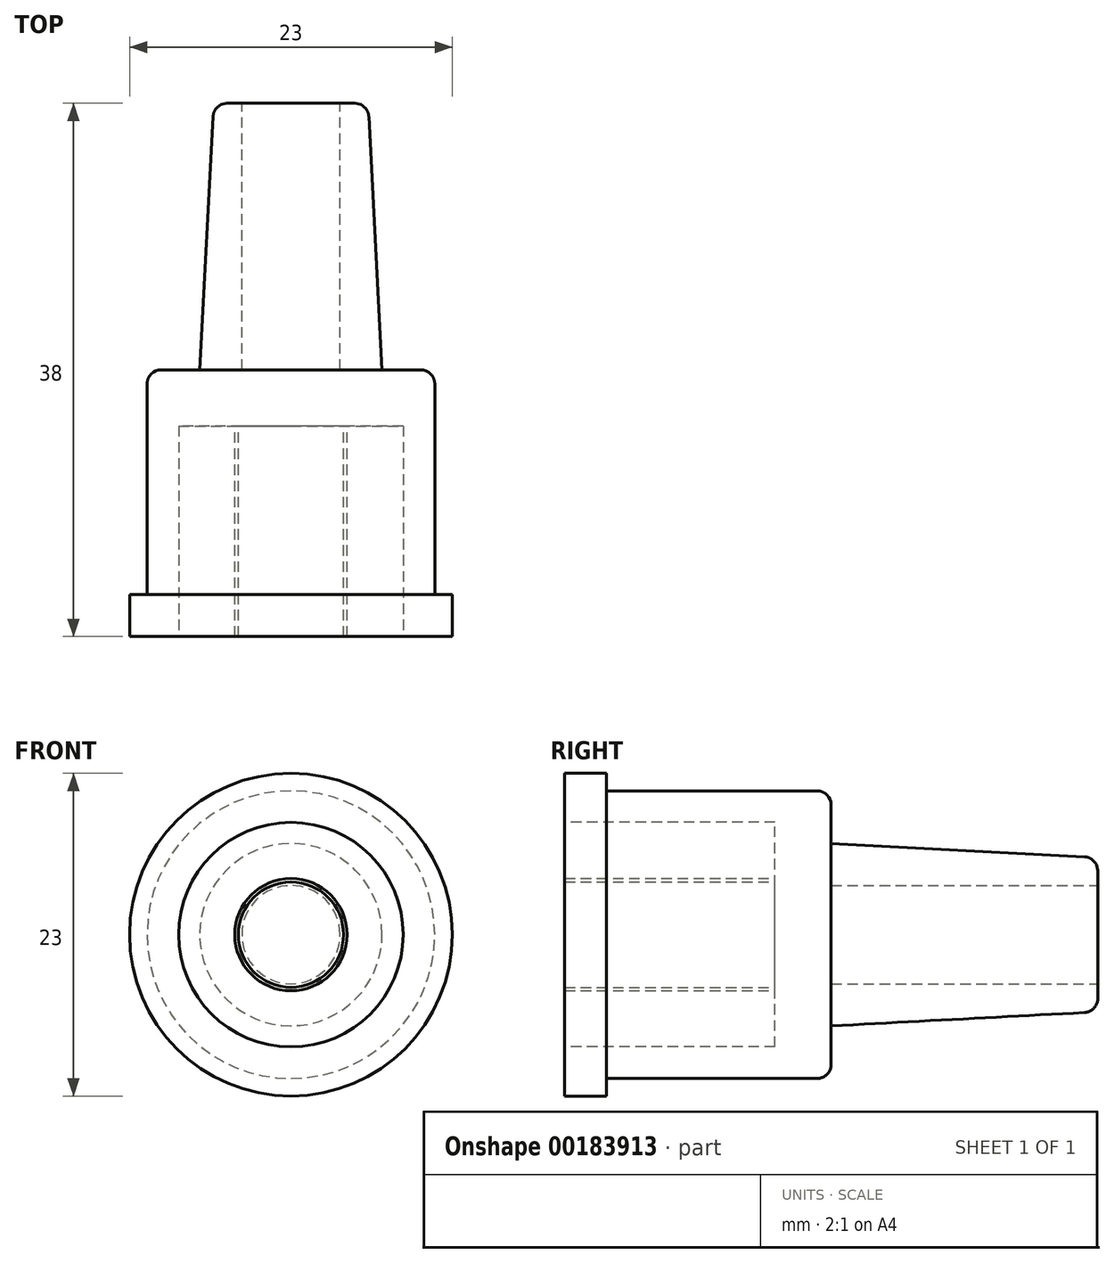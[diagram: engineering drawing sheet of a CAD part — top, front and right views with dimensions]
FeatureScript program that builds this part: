
annotation { "Feature Type Name" : "Feature", "Feature Type Description" : "" }
export const myFeature = defineFeature(function(context is Context, id is Id, definition is map)
    precondition{}
    {
        {
            var Q0;
            Q0=qCreatedBy(makeId("Front.planeOp"),FACE);
            var sketch = newSketch(context, id + "F0", { "sketchPlane" : qUnion([Q0])});
            skCircle(sketch, "E0", {"center": v(0, 0) * mm, "radius": 5.5 * mm});
            skSolve(sketch);
        }
        {
            var Q0;
            Q0=qCreatedBy(makeId("Front.planeOp"),FACE);
            cPlane(context, id + "F1", {"entities" : qUnion([Q0]), "cplaneType" : CPlaneType.OFFSET, "offset" : 19 * mm, "width" : 150 * mm, "height" : 150 * mm});
        }
        {
            var Q0;
            Q0=qCreatedBy(id+"F1.planeOp",FACE);
            var sketch = newSketch(context, id + "F2", { "sketchPlane" : qUnion([Q0])});
            skCircle(sketch, "E1", {"center": v(0, 0) * mm, "radius": 6.5 * mm});
            skSolve(sketch);
        }
        {
            var Q0;
            Q0=makeQuery(id+"F2.imprint","IMPRINT",FACE,{"disambiguationData":[TD([[makeQuery(id+"F2.imprint","IMPRINT",EDGE,{"derivedFrom":sQuery(id+"F2.wireOp",EDGE,"E1")}),1.0]])]});
            var Q1;
            Q1=makeQuery(id+"F0.imprint","IMPRINT",FACE,{"disambiguationData":[TD([[makeQuery(id+"F0.imprint","IMPRINT",EDGE,{"derivedFrom":sQuery(id+"F0.wireOp",EDGE,"E0")}),1.0]])]});
            loft(context, id + "F3", {"sheetProfilesArray" : [{ "sheetProfileEntities" : qUnion([Q0]) }, { "sheetProfileEntities" : qUnion([Q1]) }]});
        }
        {
            var Q0;
            Q0=makeQuery(id+"F3.opLoft","CAP_FACE",FACE,{"disambiguationData":[OSD([makeQuery(id+"F2.imprint","IMPRINT",FACE,{"disambiguationData":[TD([[makeQuery(id+"F2.imprint","IMPRINT",EDGE,{"derivedFrom":sQuery(id+"F2.wireOp",EDGE,"E1")}),1.0]])]})])],"isStart":true});
            var sketch = newSketch(context, id + "F4", { "sketchPlane" : qUnion([Q0])});
            skCircle(sketch, "E2", {"center": v(0, 0) * mm, "radius": 10.25 * mm});
            skSolve(sketch);
        }
        {
            var Q0;
            Q0 = qSketchRegion(id + "F4", true);
            extrude(context, id + "F5", {"entities" : qUnion([Q0]), "operationType" : NewBodyOperationType.ADD, "depth" : 19 * mm});
        }
        {
            var Q0;
            Q0=makeQuery(id+"F5.opExtrude","CAP_FACE",FACE,{"disambiguationData":[OSD([sQuery(id+"F4.wireOp",EDGE,"E2")])],"isStart":false});
            var sketch = newSketch(context, id + "F6", { "sketchPlane" : qUnion([Q0])});
            skCircle(sketch, "E3", {"center": v(0, 0) * mm, "radius": 11.5 * mm});
            skSolve(sketch);
        }
        {
            var Q0;
            Q0 = qSketchRegion(id + "F6", true);
            extrude(context, id + "F7", {"entities" : qUnion([Q0]), "operationType" : NewBodyOperationType.ADD, "oppositeDirection" : true, "depth" : 3 * mm});
        }
        {
            var Q0;
            Q0=makeQuery(id+"F3.opLoft","CAP_FACE",FACE,{"disambiguationData":[OSD([makeQuery(id+"F0.imprint","IMPRINT",FACE,{"disambiguationData":[TD([[makeQuery(id+"F0.imprint","IMPRINT",EDGE,{"derivedFrom":sQuery(id+"F0.wireOp",EDGE,"E0")}),1.0]])]})])],"isStart":true});
            var sketch = newSketch(context, id + "F8", { "sketchPlane" : qUnion([Q0])});
            skCircle(sketch, "E4", {"center": v(0, 0) * mm, "radius": 3.5 * mm});
            skSolve(sketch);
        }
        {
            var Q0;
            Q0 = qSketchRegion(id + "F8", true);
            extrude(context, id + "F9", {"entities" : qUnion([Q0]), "operationType" : NewBodyOperationType.REMOVE, "oppositeDirection" : true, "depth" : 19 * mm});
        }
        {
            var Q0;
            Q0=makeQuery(id+"F7.boolean.opBoolean","MERGE",FACE,{"derivedFrom":[makeQuery(id+"F5.opExtrude","CAP_FACE",FACE,{"disambiguationData":[OSD([sQuery(id+"F4.wireOp",EDGE,"E2")])],"isStart":false}),makeQuery(id+"F7.opExtrude","CAP_FACE",FACE,{"disambiguationData":[OSD([sQuery(id+"F6.wireOp",EDGE,"E3")])],"isStart":true})]});
            var sketch = newSketch(context, id + "F10", { "sketchPlane" : qUnion([Q0])});
            skCircle(sketch, "E5", {"center": v(0, 0) * mm, "radius": 8 * mm});
            skSolve(sketch);
        }
        {
            var Q0;
            Q0=makeQuery(id+"F10.imprint","IMPRINT",FACE,{"disambiguationData":[TD([[makeQuery(id+"F10.imprint","IMPRINT",EDGE,{"derivedFrom":sQuery(id+"F10.wireOp",EDGE,"E5")}),1.0]])]});
            extrude(context, id + "F11", {"entities" : qUnion([Q0]), "operationType" : NewBodyOperationType.REMOVE, "oppositeDirection" : true, "depth" : 15 * mm});
        }
        {
            var Q0;
            Q0=makeQuery(id+"F11.boolean.opBoolean","COPY",FACE,{"derivedFrom":makeQuery(id+"F11.opExtrude","CAP_FACE",FACE,{"disambiguationData":[OSD([sQuery(id+"F10.wireOp",EDGE,"E5")])],"isStart":false})});
            var sketch = newSketch(context, id + "F12", { "sketchPlane" : qUnion([Q0])});
            skCircle(sketch, "E6", {"center": v(0, 0) * mm, "radius": 4 * mm});
            skCircle(sketch, "E7", {"center": v(0, 0) * mm, "radius": 3.75 * mm});
            skSolve(sketch);
        }
        {
            var Q0;
            Q0=makeQuery(id+"F12.imprint","IMPRINT",FACE,{"disambiguationData":[TD([[makeQuery(id+"F12.imprint","IMPRINT",EDGE,{"derivedFrom":sQuery(id+"F12.wireOp",EDGE,"E6")}),1.0]])]});
            extrude(context, id + "F13", {"entities" : qUnion([Q0]), "depth" : 15 * mm});
        }
        {
            var Q0;
            Q0=makeQuery(id+"F3.opLoft","MID_CAP_EDGE",EDGE,{"disambiguationData":[OSD([sQuery(id+"F0.wireOp",EDGE,"E0"),sQuery(id+"F2.wireOp",EDGE,"E1")])],"capPos":1.0});
            var Q1;
            Q1=makeQuery(id+"F5.opExtrude","CAP_EDGE",EDGE,{"disambiguationData":[OSD([sQuery(id+"F4.wireOp",EDGE,"E2")])],"isStart":true});
            var Q2;
            Q2=makeQuery(id+"F3.opLoft","MID_CAP_EDGE",EDGE,{"disambiguationData":[OSD([sQuery(id+"F2.wireOp",EDGE,"E1")])],"capPos":0.0});
            fillet(context, id + "F14", {"entities" : qUnion([Q0, Q1, Q2]), "radius" : 1 * mm, "tangentPropagation" : true, "allowEdgeOverflow" : false});
        }
    });
